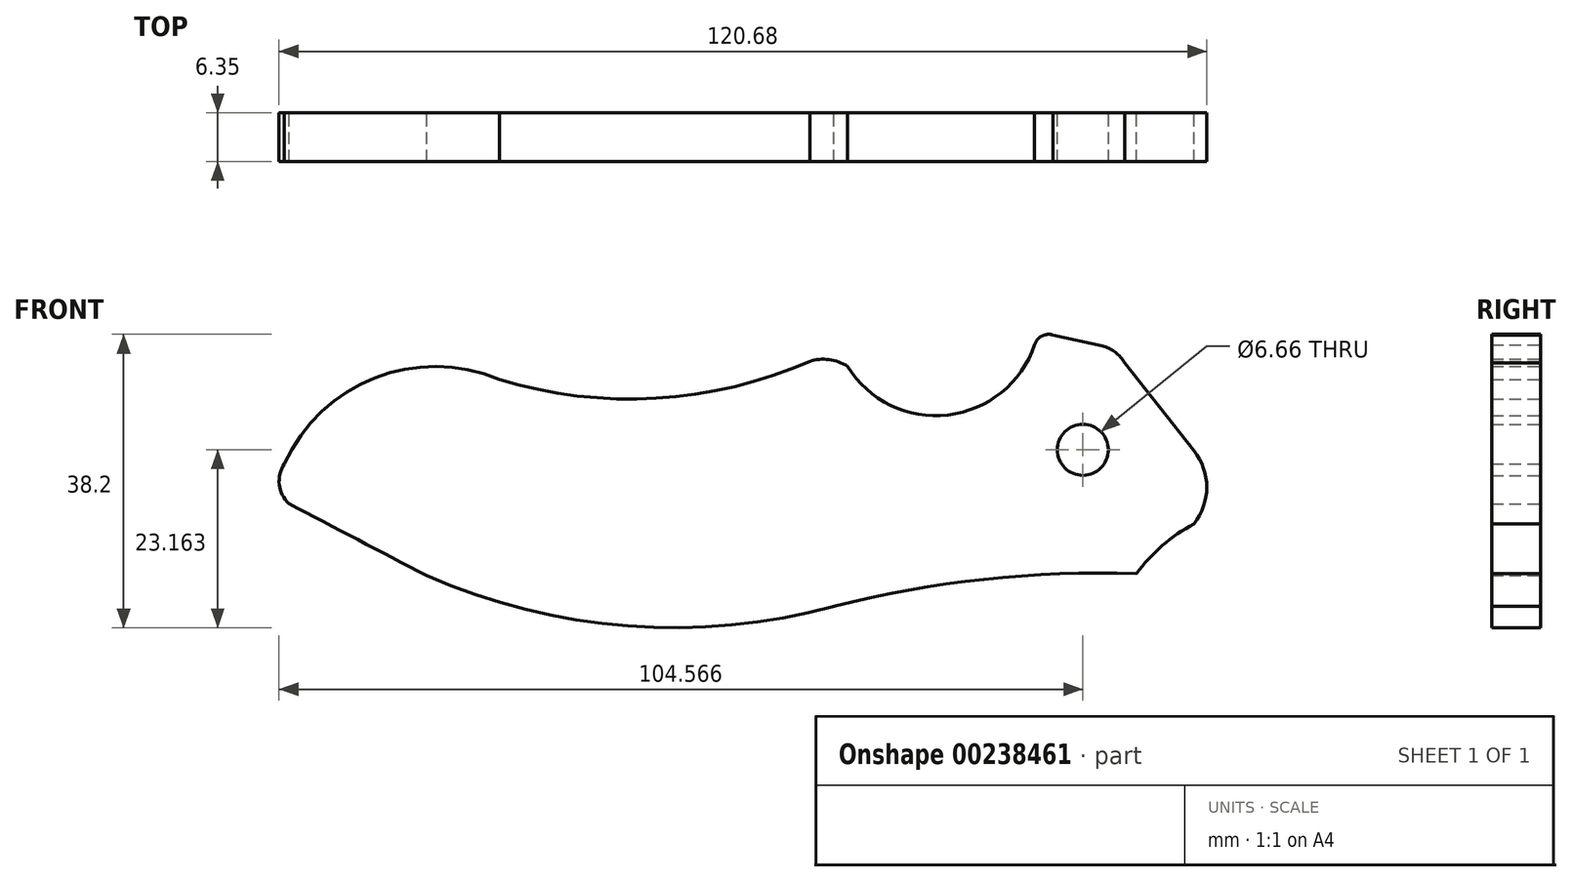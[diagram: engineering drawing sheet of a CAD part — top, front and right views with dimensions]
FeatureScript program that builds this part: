
annotation { "Feature Type Name" : "Feature", "Feature Type Description" : "" }
export const myFeature = defineFeature(function(context is Context, id is Id, definition is map)
    precondition{}
    {
        {
            var Q0;
            Q0=qCreatedBy(makeId("Front.planeOp"),FACE);
            var sketch = newSketch(context, id + "F0", { "sketchPlane" : qUnion([Q0])});
            skArc(sketch, "E0", {"start": v(-29.52, -5.48) * mm, "mid": v(-45.74, -5.26) * mm, "end": v(-57.47, -16.46) * mm});
            skArc(sketch, "E1", {"start": v(-29.52, -5.48) * mm, "mid": v(-9.12, -7.9) * mm, "end": v(10.86, -3.1) * mm});
            skArc(sketch, "E2", {"start": v(15.77, -3.74) * mm, "mid": v(13.39, -2.87) * mm, "end": v(10.86, -3.1) * mm});
            skArc(sketch, "E3", {"start": v(15.77, -3.74) * mm, "mid": v(28.83, -10.07) * mm, "end": v(40.12, -0.95) * mm});
            skArc(sketch, "E4", {"start": v(42.53, 0.33) * mm, "mid": v(41.06, 0.2) * mm, "end": v(40.12, -0.95) * mm});
            skLineSegment(sketch, "E5", {"start": v(48.91, -1.1) * mm, "end": v(42.53, 0.33) * mm});
            skLineSegment(sketch, "E6", {"start": v(51.82, -3.33) * mm, "end": v(60.86, -14.75) * mm});
            skArc(sketch, "E7", {"start": v(51.82, -3.33) * mm, "mid": v(50.61, -1.9) * mm, "end": v(48.91, -1.1) * mm});
            skArc(sketch, "E8", {"start": v(60.86, -24.25) * mm, "mid": v(62.5, -19.5) * mm, "end": v(60.86, -14.75) * mm});
            skArc(sketch, "E9", {"start": v(60.86, -24.25) * mm, "mid": v(56.74, -27.09) * mm, "end": v(53.34, -30.75) * mm});
            skArc(sketch, "E10", {"start": v(-57.47, -16.46) * mm, "mid": v(-58.15, -19.16) * mm, "end": v(-56.88, -21.64) * mm});
            skArc(sketch, "E11", {"start": v(-56.88, -21.64) * mm, "mid": v(-47.93, -26.33) * mm, "end": v(-38.96, -31) * mm});
            skArc(sketch, "E12", {"start": v(-38.96, -31) * mm, "mid": v(-12.8, -37.55) * mm, "end": v(14.03, -35) * mm});
            skArc(sketch, "E13", {"start": v(53.34, -30.75) * mm, "mid": v(33.54, -31.48) * mm, "end": v(14.03, -35) * mm});
            skPoint(sketch, "E14", {"position": v(46.4, -14.62) * mm});
            skCircle(sketch, "E15", {"center": v(46.4, -14.62) * mm, "radius": 3.33 * mm});
            skCircle(sketch, "E16", {"center": v(46.4, -14.62) * mm, "radius": 0.78 * mm});
            skSolve(sketch);
        }
        {
            var Q0;
            Q0=makeQuery(id+"F0.imprint","IMPRINT",FACE,{"disambiguationData":[TD([[makeQuery(id+"F0.imprint","IMPRINT",EDGE,{"derivedFrom":sQuery(id+"F0.wireOp",EDGE,"E0")}),1.0]])]});
            extrude(context, id + "F1", {"entities" : qUnion([Q0]), "depth" : 6.35 * mm});
        }
    });
